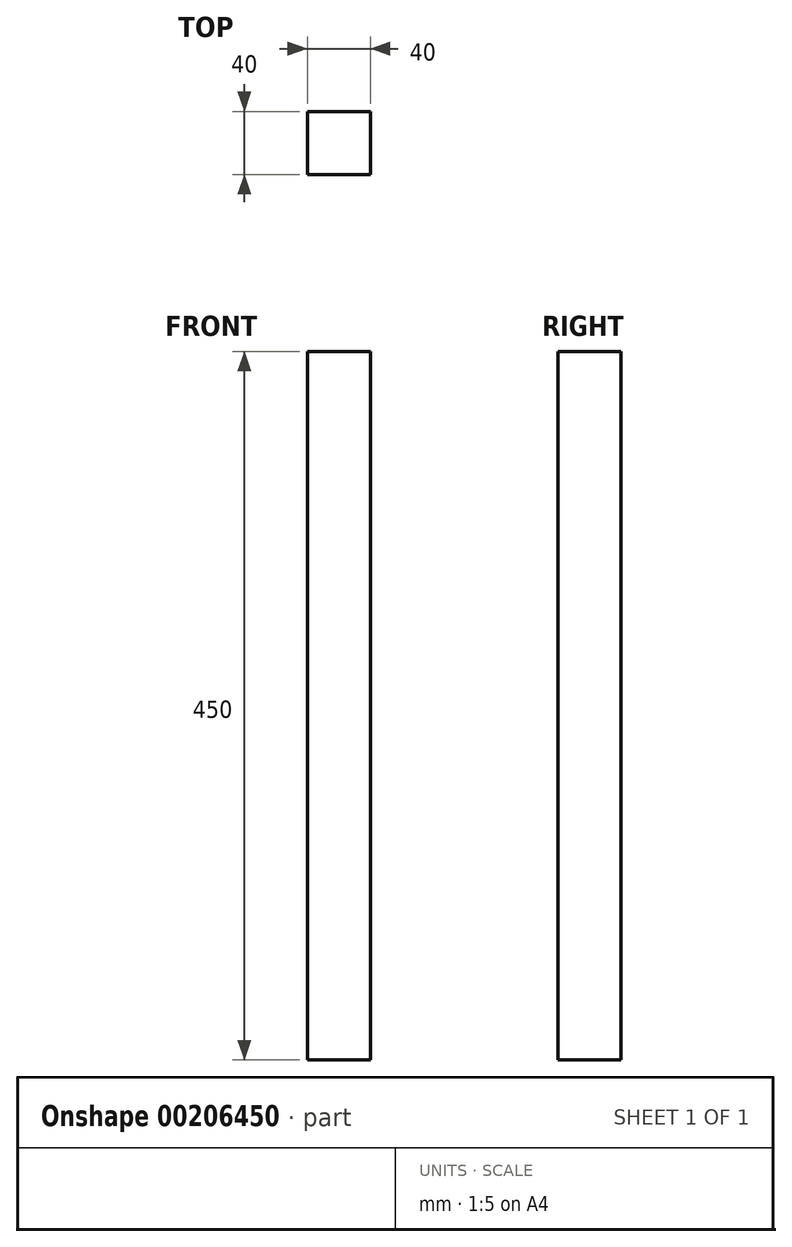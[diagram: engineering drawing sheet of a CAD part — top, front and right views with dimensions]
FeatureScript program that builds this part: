
annotation { "Feature Type Name" : "Feature", "Feature Type Description" : "" }
export const myFeature = defineFeature(function(context is Context, id is Id, definition is map)
    precondition{}
    {
        {
            var Q0;
            Q0=qCreatedBy(makeId("Top.planeOp"),FACE);
            var sketch = newSketch(context, id + "F0", { "sketchPlane" : qUnion([Q0])});
            skLineSegment(sketch, "E0.bottom", {"start": v(0, 0) * mm, "end": v(40, 0) * mm});
            skLineSegment(sketch, "E0.top", {"start": v(0, 40) * mm, "end": v(40, 40) * mm});
            skLineSegment(sketch, "E0.left", {"start": v(0, 0) * mm, "end": v(0, 40) * mm});
            skLineSegment(sketch, "E0.right", {"start": v(40, 0) * mm, "end": v(40, 40) * mm});
            skSolve(sketch);
        }
        {
            var Q0;
            Q0=makeQuery(id+"F0.imprint","IMPRINT",FACE,{"disambiguationData":[TD([[makeQuery(id+"F0.imprint","IMPRINT",EDGE,{"derivedFrom":sQuery(id+"F0.wireOp",EDGE,"E0.bottom")}),1.0]])]});
            extrude(context, id + "F1", {"entities" : qUnion([Q0]), "depth" : 450 * mm});
        }
    });
